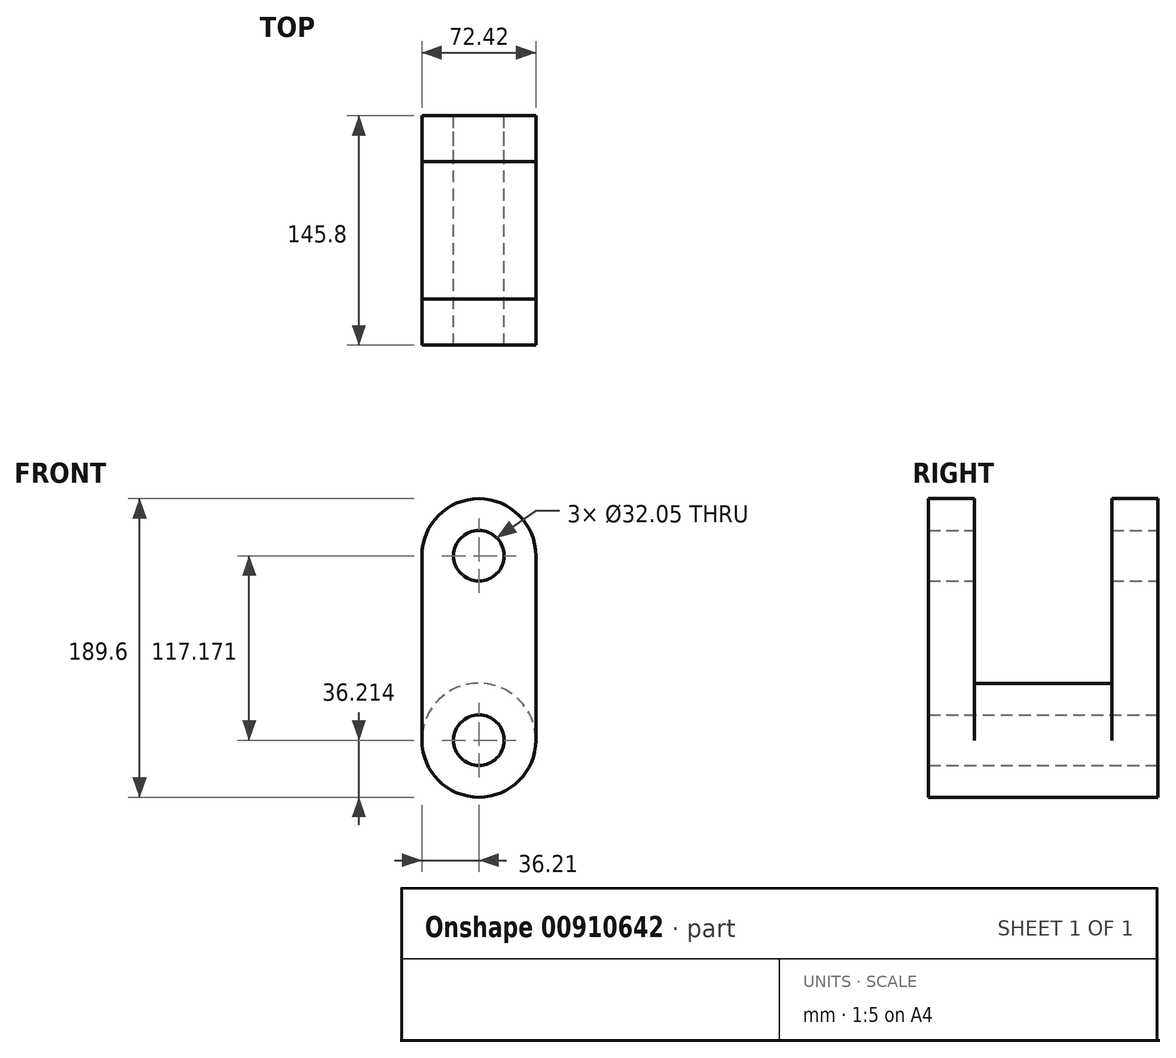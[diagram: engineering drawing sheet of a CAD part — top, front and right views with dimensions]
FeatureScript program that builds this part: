
annotation { "Feature Type Name" : "Feature", "Feature Type Description" : "" }
export const myFeature = defineFeature(function(context is Context, id is Id, definition is map)
    precondition{}
    {
        {
            var Q0;
            Q0=qCreatedBy(makeId("Front.planeOp"),FACE);
            var sketch = newSketch(context, id + "F0", { "sketchPlane" : qUnion([Q0])});
            skLineSegment(sketch, "E0.bottom", {"start": v(36.21, -58.59) * mm, "end": v(-36.21, -58.59) * mm});
            skLineSegment(sketch, "E0.top", {"start": v(36.21, 58.59) * mm, "end": v(-36.21, 58.59) * mm});
            skLineSegment(sketch, "E0.left", {"start": v(36.21, -58.59) * mm, "end": v(36.21, 58.59) * mm});
            skLineSegment(sketch, "E0.right", {"start": v(-36.21, -58.59) * mm, "end": v(-36.21, 58.59) * mm});
            skPoint(sketch, "E0.middle", {"position": v(0, 0) * mm});
            skCircle(sketch, "E1", {"center": v(0, 58.59) * mm, "radius": 36.21 * mm});
            skCircle(sketch, "E2", {"center": v(0, -58.59) * mm, "radius": 36.21 * mm});
            skCircle(sketch, "E3", {"center": v(0, 58.59) * mm, "radius": 16.02 * mm});
            skCircle(sketch, "E4", {"center": v(0, -58.59) * mm, "radius": 16.02 * mm});
            skSolve(sketch);
        }
        {
            var Q0;
            {var subQ1=sQuery(id+"F0.wireOp",EDGE,"E0.top");var subQ3=sQuery(id+"F0.wireOp",EDGE,"E3");var subQ4=makeQuery(id+"F0.imprint","INTERSECT",VERTEX,{"disambiguationData":[OD(0.0)],"derivedFrom":[subQ1,subQ3]});Q0=makeQuery(id+"F0.imprint","IMPRINT",FACE,{"disambiguationData":[TD([[makeQuery(id+"F0.imprint","IMPRINT",EDGE,{"disambiguationData":[TD([[subQ4,-1.0]])],"derivedFrom":subQ3}),-1.0]])]});}
            var Q1;
            {var subQ1=sQuery(id+"F0.wireOp",EDGE,"E0.top");var subQ3=sQuery(id+"F0.wireOp",EDGE,"E3");var subQ4=makeQuery(id+"F0.imprint","INTERSECT",VERTEX,{"disambiguationData":[OD(0.0)],"derivedFrom":[subQ1,subQ3]});Q1=makeQuery(id+"F0.imprint","IMPRINT",FACE,{"disambiguationData":[TD([[makeQuery(id+"F0.imprint","IMPRINT",EDGE,{"disambiguationData":[TD([[subQ4,1.0]])],"derivedFrom":subQ3}),-1.0]])]});}
            var Q2;
            {var subQ0=sQuery(id+"F0.wireOp",EDGE,"E0.left");Q2=makeQuery(id+"F0.imprint","IMPRINT",FACE,{"disambiguationData":[TD([[makeQuery(id+"F0.imprint","IMPRINT",EDGE,{"derivedFrom":subQ0}),1.0]])]});}
            var Q3;
            {var subQ1=sQuery(id+"F0.wireOp",EDGE,"E0.bottom");var subQ3=sQuery(id+"F0.wireOp",EDGE,"E4");var subQ4=makeQuery(id+"F0.imprint","INTERSECT",VERTEX,{"disambiguationData":[OD(0.0)],"derivedFrom":[subQ1,subQ3]});Q3=makeQuery(id+"F0.imprint","IMPRINT",FACE,{"disambiguationData":[TD([[makeQuery(id+"F0.imprint","IMPRINT",EDGE,{"disambiguationData":[TD([[subQ4,-1.0]])],"derivedFrom":subQ3}),-1.0]])]});}
            var Q4;
            {var subQ1=sQuery(id+"F0.wireOp",EDGE,"E0.bottom");var subQ3=sQuery(id+"F0.wireOp",EDGE,"E4");var subQ4=makeQuery(id+"F0.imprint","INTERSECT",VERTEX,{"disambiguationData":[OD(0.0)],"derivedFrom":[subQ1,subQ3]});Q4=makeQuery(id+"F0.imprint","IMPRINT",FACE,{"disambiguationData":[TD([[makeQuery(id+"F0.imprint","IMPRINT",EDGE,{"disambiguationData":[TD([[subQ4,1.0]])],"derivedFrom":subQ3}),-1.0]])]});}
            extrude(context, id + "F1", {"entities" : qUnion([Q0, Q1, Q2, Q3, Q4]), "endBound" : BoundingType.SYMMETRIC, "depth" : 145.8 * mm});
        }
        {
            var Q0;
            {var subQ1=sQuery(id+"F0.wireOp",EDGE,"E0.top");var subQ3=sQuery(id+"F0.wireOp",EDGE,"E3");var subQ4=makeQuery(id+"F0.imprint","INTERSECT",VERTEX,{"disambiguationData":[OD(0.0)],"derivedFrom":[subQ1,subQ3]});Q0=makeQuery(id+"F0.imprint","IMPRINT",FACE,{"disambiguationData":[TD([[makeQuery(id+"F0.imprint","IMPRINT",EDGE,{"disambiguationData":[TD([[subQ4,-1.0]])],"derivedFrom":subQ3}),-1.0]])]});}
            var Q1;
            {var subQ1=sQuery(id+"F0.wireOp",EDGE,"E0.top");var subQ3=sQuery(id+"F0.wireOp",EDGE,"E3");var subQ4=makeQuery(id+"F0.imprint","INTERSECT",VERTEX,{"disambiguationData":[OD(0.0)],"derivedFrom":[subQ1,subQ3]});Q1=makeQuery(id+"F0.imprint","IMPRINT",FACE,{"disambiguationData":[TD([[makeQuery(id+"F0.imprint","IMPRINT",EDGE,{"disambiguationData":[TD([[subQ4,1.0]])],"derivedFrom":subQ3}),-1.0]])]});}
            var Q2;
            {var subQ0=sQuery(id+"F0.wireOp",EDGE,"E0.left");Q2=makeQuery(id+"F0.imprint","IMPRINT",FACE,{"disambiguationData":[TD([[makeQuery(id+"F0.imprint","IMPRINT",EDGE,{"derivedFrom":subQ0}),1.0]])]});}
            extrude(context, id + "F2", {"entities" : qUnion([Q0, Q1, Q2]), "operationType" : NewBodyOperationType.REMOVE, "endBound" : BoundingType.SYMMETRIC, "oppositeDirection" : true, "depth" : 87.38 * mm});
        }
    });
